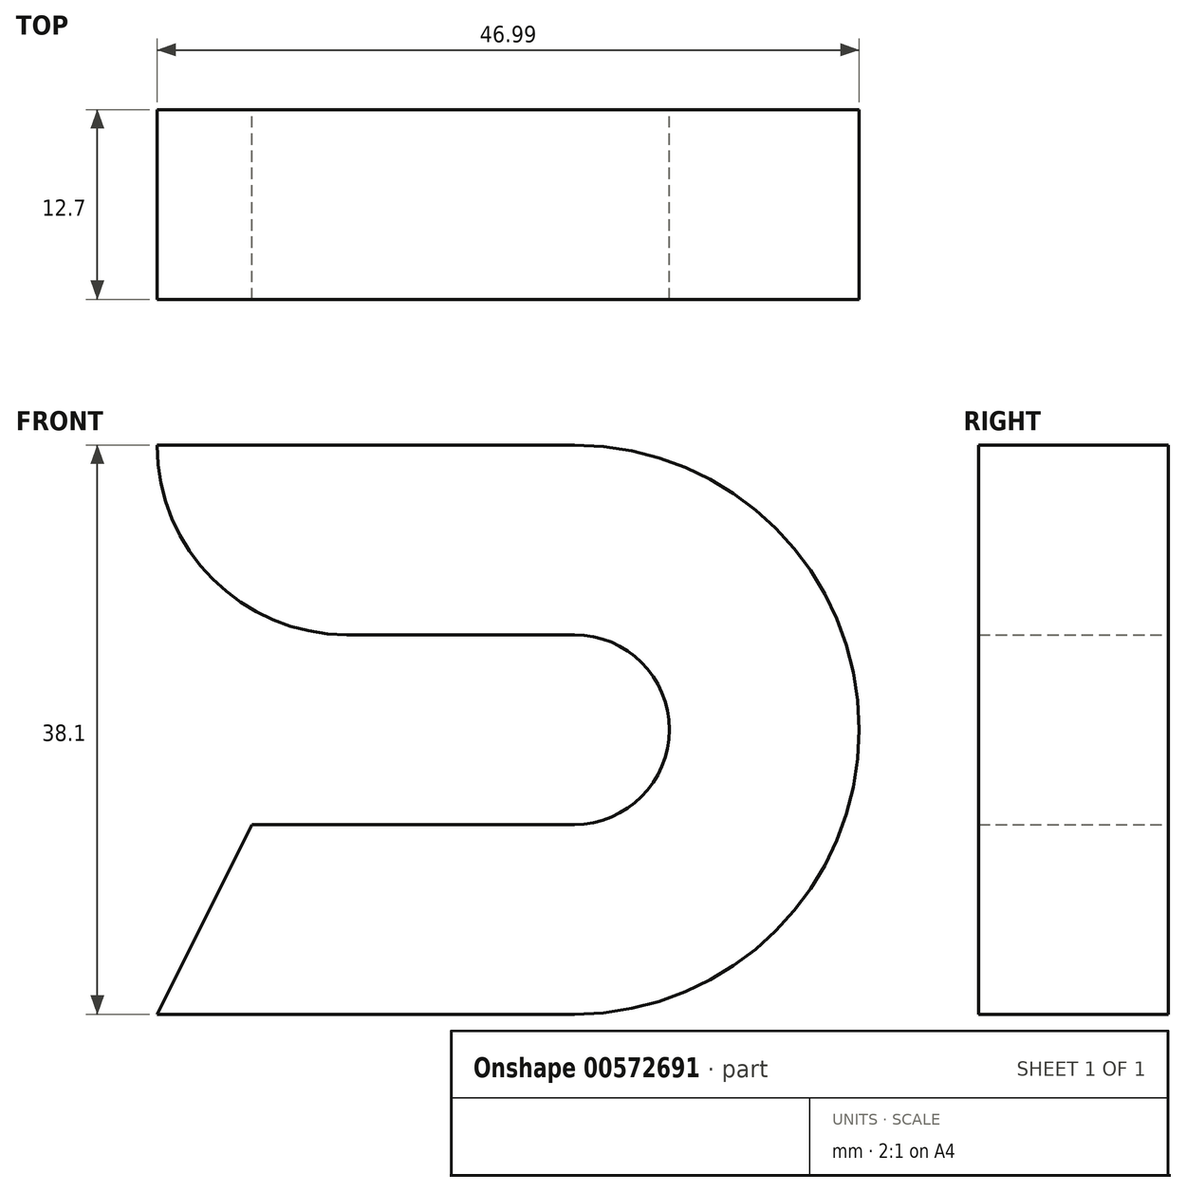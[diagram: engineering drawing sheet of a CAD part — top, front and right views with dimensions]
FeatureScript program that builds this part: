
annotation { "Feature Type Name" : "Feature", "Feature Type Description" : "" }
export const myFeature = defineFeature(function(context is Context, id is Id, definition is map)
    precondition{}
    {
        {
            var Q0;
            Q0=qCreatedBy(makeId("Front.planeOp"),FACE);
            var sketch = newSketch(context, id + "F0", { "sketchPlane" : qUnion([Q0])});
            skLineSegment(sketch, "E0", {"start": v(-17.9, 0) * mm, "end": v(10.04, 0) * mm});
            skLineSegment(sketch, "E1", {"start": v(10.04, 0) * mm, "end": v(10.04, 12.7) * mm});
            skLineSegment(sketch, "E2", {"start": v(10.04, 12.7) * mm, "end": v(-11.55, 12.7) * mm});
            skLineSegment(sketch, "E3", {"start": v(10.04, 25.4) * mm, "end": v(-5.2, 25.4) * mm});
            skLineSegment(sketch, "E4", {"start": v(-5.2, 38.1) * mm, "end": v(10.04, 38.1) * mm});
            skLineSegment(sketch, "E5", {"start": v(10.04, 25.4) * mm, "end": v(10.04, 38.1) * mm});
            skLineSegment(sketch, "E6", {"start": v(-5.2, 38.1) * mm, "end": v(-5.2, 25.4) * mm});
            skLineSegment(sketch, "E7", {"start": v(-17.9, 38.1) * mm, "end": v(-5.2, 38.1) * mm});
            skLineSegment(sketch, "E8", {"start": v(-11.55, 12.7) * mm, "end": v(-17.9, 0) * mm});
            skArc(sketch, "E9", {"start": v(10.04, 0) * mm, "mid": v(29.1, 19.05) * mm, "end": v(10.04, 38.1) * mm});
            skArc(sketch, "E10", {"start": v(-17.9, 38.1) * mm, "mid": v(-14.18, 29.12) * mm, "end": v(-5.2, 25.4) * mm});
            skArc(sketch, "E11", {"start": v(10.04, 12.7) * mm, "mid": v(16.4, 19.05) * mm, "end": v(10.04, 25.4) * mm});
            skSolve(sketch);
        }
        {
            var Q0;
            Q0=makeQuery(id+"F0.imprint","IMPRINT",FACE,{"disambiguationData":[TD([[makeQuery(id+"F0.imprint","IMPRINT",EDGE,{"derivedFrom":sQuery(id+"F0.wireOp",EDGE,"E0")}),1.0]])]});
            var Q1;
            Q1=makeQuery(id+"F0.imprint","IMPRINT",FACE,{"disambiguationData":[TD([[makeQuery(id+"F0.imprint","IMPRINT",EDGE,{"derivedFrom":sQuery(id+"F0.wireOp",EDGE,"E1")}),-1.0]])]});
            var Q2;
            Q2=makeQuery(id+"F0.imprint","IMPRINT",FACE,{"disambiguationData":[TD([[makeQuery(id+"F0.imprint","IMPRINT",EDGE,{"derivedFrom":sQuery(id+"F0.wireOp",EDGE,"Fp64eYVW-mB1R-QKNj-lSmg-RRRf5Vuwo6Hn")}),1.0]])]});
            var Q3;
            {var subQ0=sQuery(id+"F0.wireOp",EDGE,"E3");Q3=makeQuery(id+"F0.imprint","IMPRINT",FACE,{"disambiguationData":[TD([[makeQuery(id+"F0.imprint","IMPRINT",EDGE,{"derivedFrom":subQ0}),-1.0]])]});}
            var Q4;
            Q4=makeQuery(id+"F0.imprint","IMPRINT",FACE,{"disambiguationData":[TD([[makeQuery(id+"F0.imprint","IMPRINT",EDGE,{"derivedFrom":sQuery(id+"F0.wireOp",EDGE,"E6")}),-1.0]])]});
            extrude(context, id + "F1", {"entities" : qUnion([Q0, Q1, Q2, Q3, Q4]), "endBound" : BoundingType.SYMMETRIC, "depth" : 12.7 * mm, "offsetDistance" : 25.4 * mm});
        }
    });
